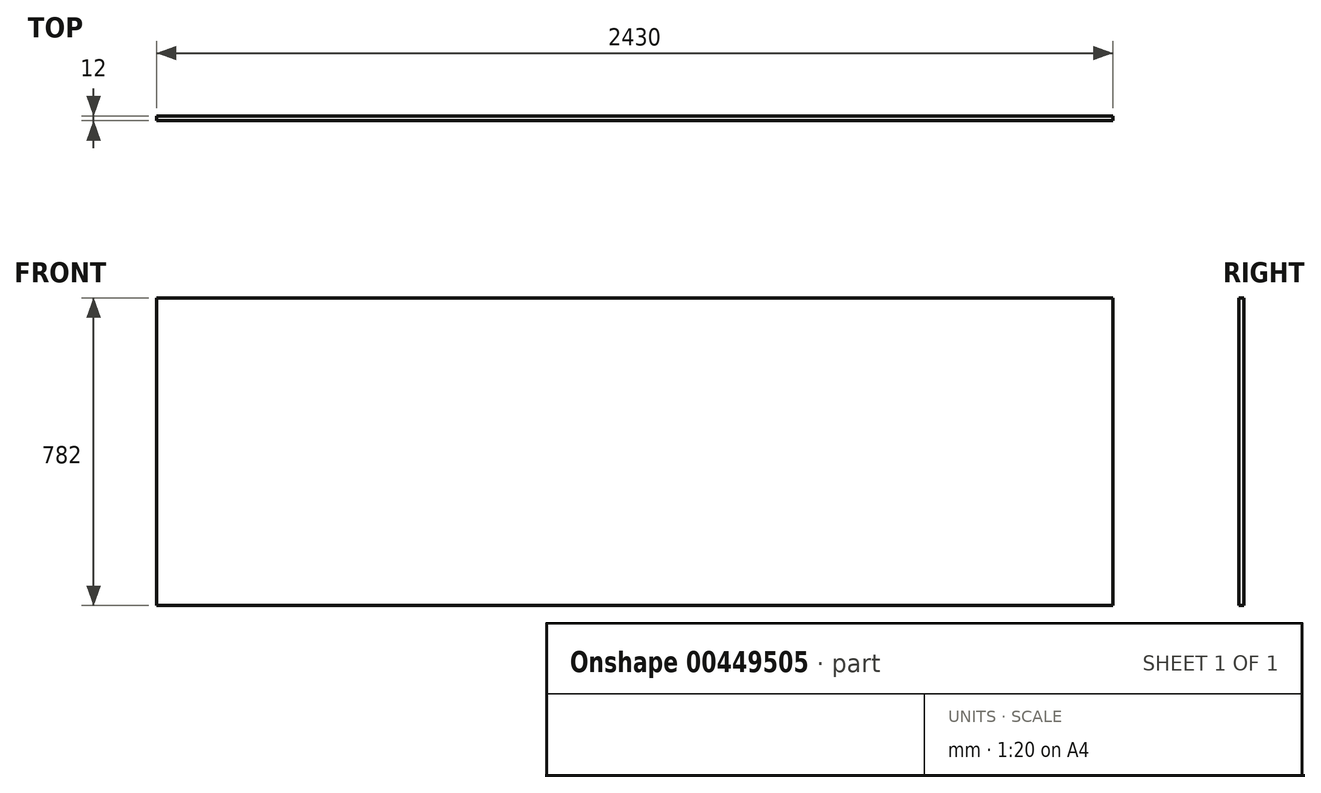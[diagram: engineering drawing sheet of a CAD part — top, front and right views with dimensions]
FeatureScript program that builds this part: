
annotation { "Feature Type Name" : "Feature", "Feature Type Description" : "" }
export const myFeature = defineFeature(function(context is Context, id is Id, definition is map)
    precondition{}
    {
        {
            var Q0;
            Q0=qCreatedBy(makeId("Front.planeOp"),FACE);
            var sketch = newSketch(context, id + "F0", { "sketchPlane" : qUnion([Q0])});
            skLineSegment(sketch, "E0.bottom", {"start": v(0, 782) * mm, "end": v(2430, 782) * mm});
            skLineSegment(sketch, "E0.top", {"start": v(0, 0) * mm, "end": v(2430, 0) * mm});
            skLineSegment(sketch, "E0.left", {"start": v(0, 782) * mm, "end": v(0, 0) * mm});
            skLineSegment(sketch, "E0.right", {"start": v(2430, 782) * mm, "end": v(2430, 0) * mm});
            skSolve(sketch);
        }
        {
            var Q0;
            Q0=qSketchRegion(id+"F0",true);
            extrude(context, id + "F1", {"entities" : qUnion([Q0]), "oppositeDirection" : true, "depth" : 12 * mm});
        }
    });
